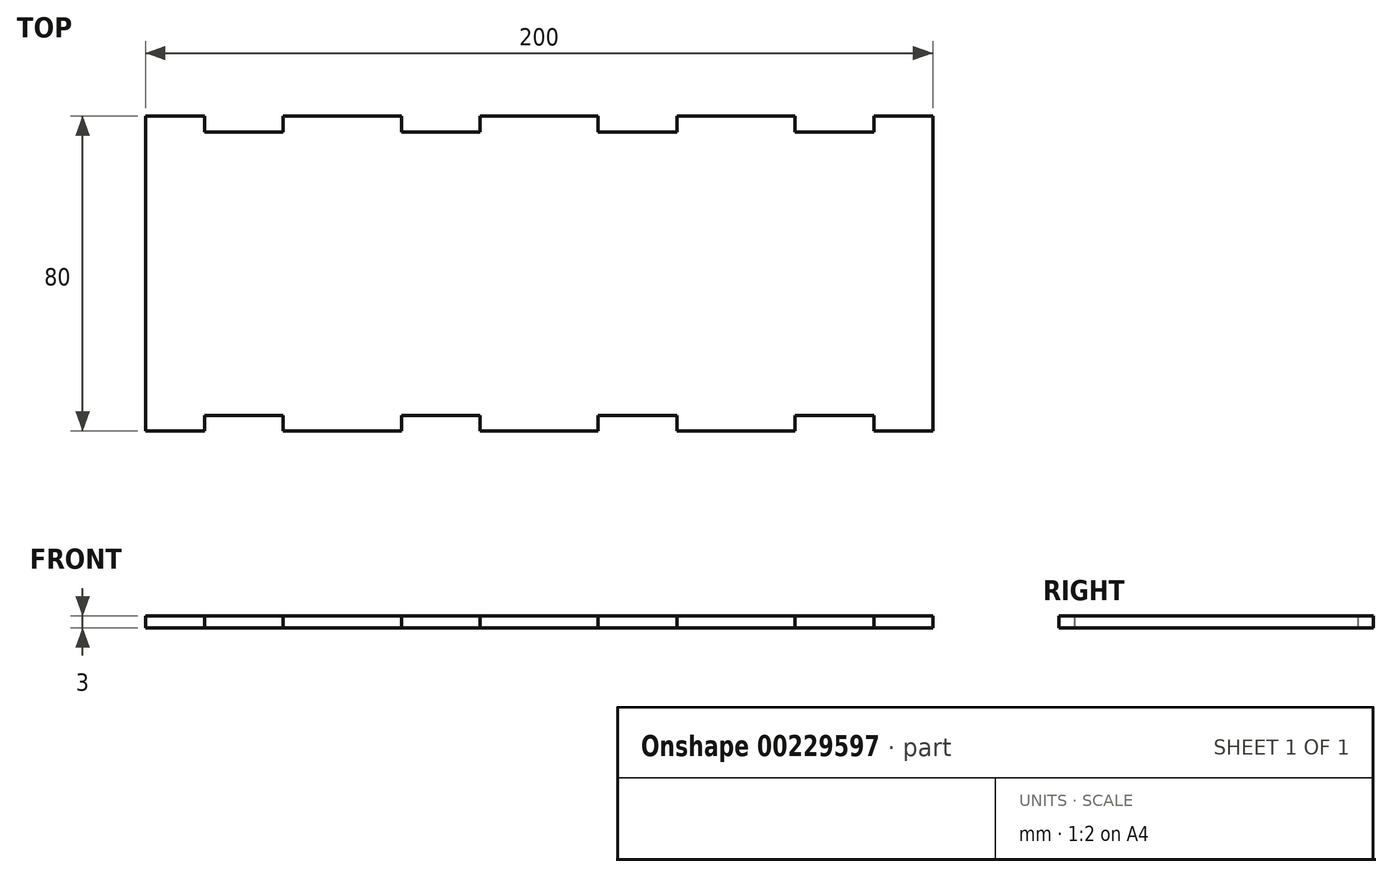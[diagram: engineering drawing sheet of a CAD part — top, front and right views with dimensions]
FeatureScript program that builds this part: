
annotation { "Feature Type Name" : "Feature", "Feature Type Description" : "" }
export const myFeature = defineFeature(function(context is Context, id is Id, definition is map)
    precondition{}
    {
        {
            var Q0;
            Q0=qCreatedBy(makeId("Top.planeOp"),FACE);
            var sketch = newSketch(context, id + "F0", { "sketchPlane" : qUnion([Q0])});
            skLineSegment(sketch, "E0.bottom", {"start": v(100, -40) * mm, "end": v(85, -40) * mm});
            skLineSegment(sketch, "E0.top", {"start": v(100, 40) * mm, "end": v(85, 40) * mm});
            skLineSegment(sketch, "E0.left", {"start": v(100, -40) * mm, "end": v(100, 40) * mm});
            skLineSegment(sketch, "E0.right", {"start": v(-100, -40) * mm, "end": v(-100, 40) * mm});
            skPoint(sketch, "E0.middle", {"position": v(0, 0) * mm});
            skLineSegment(sketch, "E1.top", {"start": v(-85, 36) * mm, "end": v(-65, 36) * mm});
            skLineSegment(sketch, "E1.left", {"start": v(-85, 40) * mm, "end": v(-85, 36) * mm});
            skLineSegment(sketch, "E1.right", {"start": v(-65, 40) * mm, "end": v(-65, 36) * mm});
            skLineSegment(sketch, "E2.top", {"start": v(-35, 36) * mm, "end": v(-15, 36) * mm});
            skLineSegment(sketch, "E2.left", {"start": v(-35, 40) * mm, "end": v(-35, 36) * mm});
            skLineSegment(sketch, "E2.right", {"start": v(-15, 40) * mm, "end": v(-15, 36) * mm});
            skLineSegment(sketch, "E3.trimOffspring", {"start": v(-85, 40) * mm, "end": v(-100, 40) * mm});
            skLineSegment(sketch, "E4.trimOffspring", {"start": v(-35, 40) * mm, "end": v(-65, 40) * mm});
            skLineSegment(sketch, "E5.MirrorCS", {"start": v(15, 40) * mm, "end": v(15, 36) * mm});
            skLineSegment(sketch, "E6.MirrorCS", {"start": v(35, 36) * mm, "end": v(15, 36) * mm});
            skLineSegment(sketch, "E7.MirrorCS", {"start": v(35, 40) * mm, "end": v(35, 36) * mm});
            skLineSegment(sketch, "E8.MirrorCS", {"start": v(65, 40) * mm, "end": v(65, 36) * mm});
            skLineSegment(sketch, "E9.MirrorCS", {"start": v(85, 40) * mm, "end": v(85, 36) * mm});
            skLineSegment(sketch, "E10.MirrorCS", {"start": v(85, 36) * mm, "end": v(65, 36) * mm});
            skLineSegment(sketch, "E11.trimOffspring", {"start": v(15, 40) * mm, "end": v(-15, 40) * mm});
            skLineSegment(sketch, "E12.trimOffspring", {"start": v(65, 40) * mm, "end": v(35, 40) * mm});
            skLineSegment(sketch, "E13.MirrorCS", {"start": v(85, -40) * mm, "end": v(85, -36) * mm});
            skLineSegment(sketch, "E14.MirrorCS", {"start": v(35, -40) * mm, "end": v(35, -36) * mm});
            skLineSegment(sketch, "E15.MirrorCS", {"start": v(65, -40) * mm, "end": v(65, -36) * mm});
            skLineSegment(sketch, "E16.MirrorCS", {"start": v(15, -40) * mm, "end": v(15, -36) * mm});
            skLineSegment(sketch, "E17.MirrorCS", {"start": v(-15, -40) * mm, "end": v(-15, -36) * mm});
            skLineSegment(sketch, "E18.MirrorCS", {"start": v(-35, -40) * mm, "end": v(-35, -36) * mm});
            skLineSegment(sketch, "E19.MirrorCS", {"start": v(-85, -40) * mm, "end": v(-85, -36) * mm});
            skLineSegment(sketch, "E20.MirrorCS", {"start": v(-65, -40) * mm, "end": v(-65, -36) * mm});
            skLineSegment(sketch, "E21.MirrorCS", {"start": v(85, -36) * mm, "end": v(65, -36) * mm});
            skLineSegment(sketch, "E22.MirrorCS", {"start": v(35, -36) * mm, "end": v(15, -36) * mm});
            skLineSegment(sketch, "E23.MirrorCS", {"start": v(-35, -36) * mm, "end": v(-15, -36) * mm});
            skLineSegment(sketch, "E24.MirrorCS", {"start": v(-85, -36) * mm, "end": v(-65, -36) * mm});
            skLineSegment(sketch, "E25.trimOffspring", {"start": v(-85, -40) * mm, "end": v(-100, -40) * mm});
            skLineSegment(sketch, "E26.trimOffspring", {"start": v(-35, -40) * mm, "end": v(-65, -40) * mm});
            skLineSegment(sketch, "E27.trimOffspring", {"start": v(15, -40) * mm, "end": v(-15, -40) * mm});
            skLineSegment(sketch, "E28.trimOffspring", {"start": v(65, -40) * mm, "end": v(35, -40) * mm});
            skSolve(sketch);
        }
        {
            var Q0;
            Q0=makeQuery(id+"F0.imprint","IMPRINT",FACE,{"disambiguationData":[TD([[makeQuery(id+"F0.imprint","IMPRINT",EDGE,{"derivedFrom":sQuery(id+"F0.wireOp",EDGE,"E0.bottom")}),-1.0]])]});
            extrude(context, id + "F1", {"entities" : qUnion([Q0]), "depth" : 3 * mm});
        }
    });
